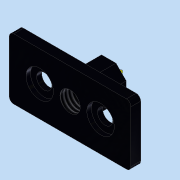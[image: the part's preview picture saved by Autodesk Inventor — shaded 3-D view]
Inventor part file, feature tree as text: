
AUTODESK INVENTOR PART (.ipt)
format: ipt  version: 2013 SP2 (Build 170200200, 200)  size: 128,000 bytes
history: native  units: mm
features: sketch x4, extrude x2, hole x2, fillet x1
ambient origin geometry x8: Origin, YZ Plane, XZ Plane, XY Plane, X Axis, Y Axis, Z Axis, Center Point
bodies: Solid1 (feature_tree)
feature tree (9):
  extrude  "Extrusion1"  Depth=20.0mm
  hole  "Hole1"  [1 undecoded]
  extrude  "Extrusion2"  Depth=10.0mm
  hole  "Hole2"  [1 undecoded]
  fillet  "Fillet1"  Radius=9.5mm
  sketch  "Sketch1"  dims[d0=40.0mm d1=20.0mm]
  sketch  "Sketch2"  dims[d2=3.2mm d3=0.0mm d4=10.0mm]
  sketch  "Sketch3"  dims[d5=20.0mm d6=10.0mm]
  sketch  "Sketch4"  dims[d7=5.0mm d8=6.0mm d9=9.0mm d10=1.5mm d11=90.0deg d12=8.0mm d13=20.594885mm d14=11.48mm d15=9.5mm d16=0.0mm d17=6.647mm d18=20.0mm d19=9.0mm d20=1.5mm d21=90.0deg d22=8.0mm d23=20.594885mm d24=1.5mm]
note: 2 required parameter values undecoded (feature->parameter linkage not recoverable at this tier; creation-order binding heuristic only, values carry confidence <= 0.55)
